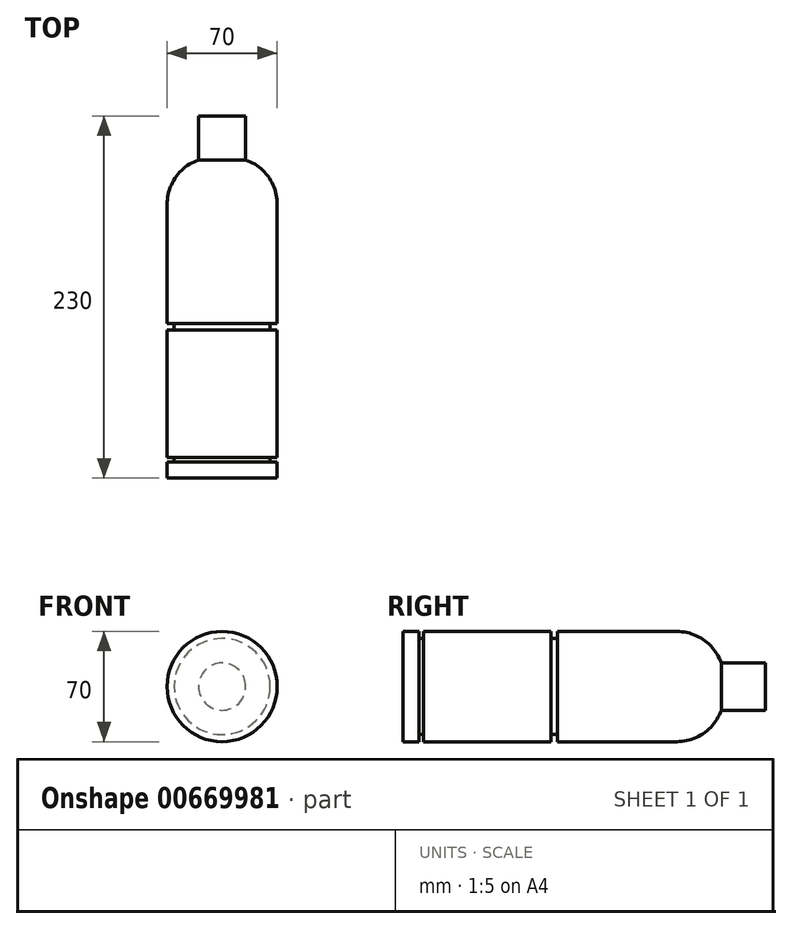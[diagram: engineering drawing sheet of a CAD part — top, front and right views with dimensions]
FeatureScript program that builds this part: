
annotation { "Feature Type Name" : "Feature", "Feature Type Description" : "" }
export const myFeature = defineFeature(function(context is Context, id is Id, definition is map)
    precondition{}
    {
        {
            var Q0;
            Q0=qCreatedBy(makeId("Front.planeOp"),FACE);
            var sketch = newSketch(context, id + "F0", { "sketchPlane" : qUnion([Q0])});
            skCircle(sketch, "E0", {"center": v(0, 0) * mm, "radius": 35 * mm});
            skSolve(sketch);
        }
        {
            var Q0;
            Q0 = qSketchRegion(id + "F0", true);
            extrude(context, id + "F1", {"entities" : qUnion([Q0]), "oppositeDirection" : true, "depth" : 230 * mm, "offsetDistance" : 25 * mm});
        }
        {
            var Q0;
            Q0=makeQuery(id+"F1.opExtrude","CAP_FACE",FACE,{"disambiguationData":[OSD([sQuery(id+"F0.wireOp",EDGE,"E0")])],"isStart":true});
            cPlane(context, id + "F2", {"entities" : qUnion([Q0]), "cplaneType" : CPlaneType.OFFSET, "offset" : 10 * mm, "oppositeDirection" : true, "width" : 150 * mm, "height" : 150 * mm});
        }
        {
            var Q0;
            Q0=qCreatedBy(id+"F2.planeOp",FACE);
            var sketch = newSketch(context, id + "F3", { "sketchPlane" : qUnion([Q0])});
            skCircle(sketch, "E1", {"center": v(0, 0) * mm, "radius": 30.5 * mm});
            skCircle(sketch, "E2", {"center": v(0, 0) * mm, "radius": 40.5 * mm});
            skSolve(sketch);
        }
        {
            var Q0;
            Q0 = qSketchRegion(id + "F3", true);
            extrude(context, id + "F4", {"entities" : qUnion([Q0]), "operationType" : NewBodyOperationType.REMOVE, "oppositeDirection" : true, "depth" : 3 * mm, "offsetDistance" : 25 * mm});
        }
        {
            var Q0;
            Q0=makeQuery(id+"F1.opExtrude","CAP_FACE",FACE,{"disambiguationData":[OSD([sQuery(id+"F0.wireOp",EDGE,"E0")])],"isStart":true});
            cPlane(context, id + "F5", {"entities" : qUnion([Q0]), "cplaneType" : CPlaneType.OFFSET, "offset" : 94 * mm, "oppositeDirection" : true, "width" : 150 * mm, "height" : 150 * mm});
        }
        {
            var Q0;
            Q0=qCreatedBy(id+"F5.planeOp",FACE);
            var sketch = newSketch(context, id + "F6", { "sketchPlane" : qUnion([Q0])});
            skCircle(sketch, "E3", {"center": v(0, 0) * mm, "radius": 30.5 * mm});
            skCircle(sketch, "E4", {"center": v(0, 0) * mm, "radius": 40 * mm});
            skSolve(sketch);
        }
        {
            var Q0;
            Q0 = qSketchRegion(id + "F6", true);
            extrude(context, id + "F7", {"entities" : qUnion([Q0]), "operationType" : NewBodyOperationType.REMOVE, "oppositeDirection" : true, "depth" : 4 * mm, "offsetDistance" : 25 * mm});
        }
        {
            var Q0;
            Q0=makeQuery(id+"F1.opExtrude","CAP_FACE",FACE,{"disambiguationData":[OSD([sQuery(id+"F0.wireOp",EDGE,"E0")])],"isStart":false});
            var sketch = newSketch(context, id + "F8", { "sketchPlane" : qUnion([Q0])});
            skCircle(sketch, "E5", {"center": v(0, 0) * mm, "radius": 15 * mm});
            skCircle(sketch, "E6", {"center": v(0, 0) * mm, "radius": 40 * mm});
            skSolve(sketch);
        }
        {
            var Q0;
            Q0 = qSketchRegion(id + "F8", true);
            extrude(context, id + "F9", {"entities" : qUnion([Q0]), "operationType" : NewBodyOperationType.REMOVE, "oppositeDirection" : true, "depth" : 28 * mm, "offsetDistance" : 25 * mm});
        }
        {
            var Q0;
            {var subQ0=sQuery(id+"F0.wireOp",EDGE,"E0");var subQ1=makeQuery(id+"F1.opExtrude","CAP_FACE",FACE,{"disambiguationData":[OSD([subQ0])],"isStart":false});Q0=makeQuery(id+"F9.boolean.opBoolean","INTERSECT",EDGE,{"derivedFrom":[makeQuery(id+"F7.boolean.opBoolean","SPLIT",FACE,{"disambiguationData":[TD([subQ1])],"derivedFrom":makeQuery(id+"F4.boolean.opBoolean","SPLIT",FACE,{"disambiguationData":[TD([subQ1])],"derivedFrom":makeQuery(id+"F1.opExtrude","SWEPT_FACE",FACE,{"disambiguationData":[OSD([subQ0])]})})}),makeQuery(id+"F9.opExtrude","CAP_FACE",FACE,{"disambiguationData":[OSD([sQuery(id+"F8.wireOp",EDGE,"E5"),sQuery(id+"F8.wireOp",EDGE,"E6")])],"isStart":false})]});}
            fillet(context, id + "F10", {"entities" : qUnion([Q0]), "radius" : 30 * mm, "tangentPropagation" : true, "allowEdgeOverflow" : false});
        }
    });
